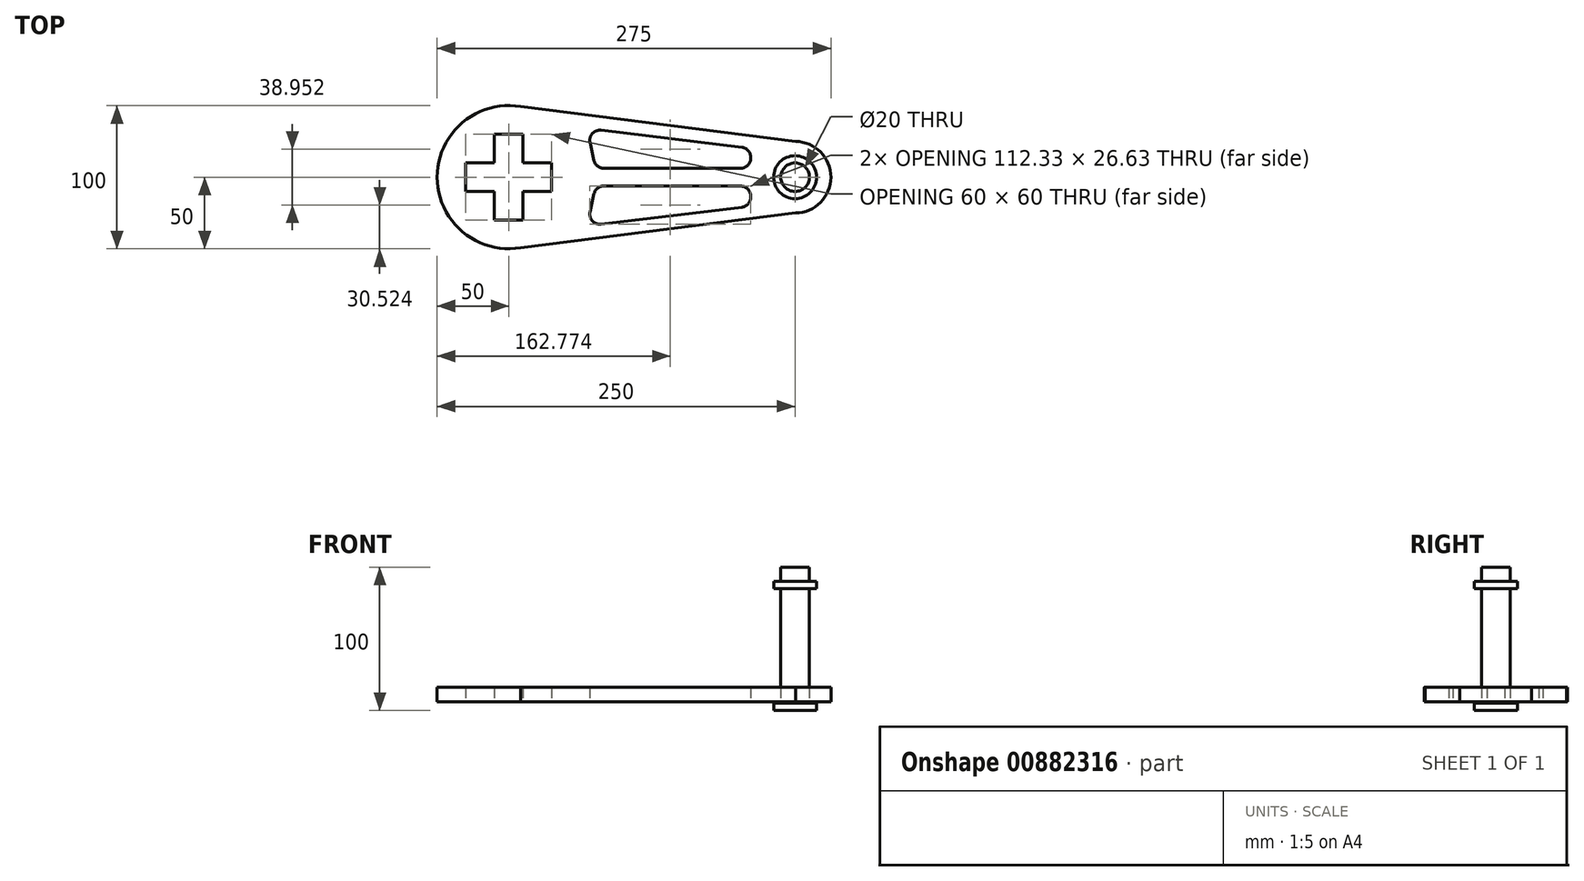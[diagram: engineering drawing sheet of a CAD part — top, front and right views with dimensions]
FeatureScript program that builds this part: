
annotation { "Feature Type Name" : "Feature", "Feature Type Description" : "" }
export const myFeature = defineFeature(function(context is Context, id is Id, definition is map)
    precondition{}
    {
        {
            var Q0;
            Q0=qCreatedBy(makeId("Top.planeOp"),FACE);
            var sketch = newSketch(context, id + "F0", { "sketchPlane" : qUnion([Q0])});
            skCircle(sketch, "E0", {"center": v(0, 0) * mm, "radius": 50 * mm});
            skLineSegment(sketch, "E1", {"start": v(0, 0) * mm, "end": v(0, 30) * mm, "construction": true});
            skLineSegment(sketch, "E2", {"start": v(0, 0) * mm, "end": v(-33.4, 0) * mm, "construction": true});
            skLineSegment(sketch, "E3", {"start": v(0, 30) * mm, "end": v(-10, 30) * mm});
            skLineSegment(sketch, "E4", {"start": v(-10, 30) * mm, "end": v(-10, 10) * mm});
            skLineSegment(sketch, "E5", {"start": v(-10, 10) * mm, "end": v(-30, 10) * mm});
            skLineSegment(sketch, "E6", {"start": v(-30, 10) * mm, "end": v(-30, 0) * mm});
            skLineSegment(sketch, "E7.MirrorCS", {"start": v(0, 30) * mm, "end": v(10, 30) * mm});
            skLineSegment(sketch, "E8.MirrorCS", {"start": v(10, 30) * mm, "end": v(10, 10) * mm});
            skLineSegment(sketch, "E9.MirrorCS", {"start": v(10, 10) * mm, "end": v(30, 10) * mm});
            skLineSegment(sketch, "E10.MirrorCS", {"start": v(30, 10) * mm, "end": v(30, 0) * mm});
            skLineSegment(sketch, "E11.MirrorCS", {"start": v(-30, -10) * mm, "end": v(-30, 0) * mm});
            skLineSegment(sketch, "E12.MirrorCS", {"start": v(-10, -10) * mm, "end": v(-30, -10) * mm});
            skLineSegment(sketch, "E13.MirrorCS", {"start": v(-10, -30) * mm, "end": v(-10, -10) * mm});
            skLineSegment(sketch, "E14.MirrorCS", {"start": v(0, -30) * mm, "end": v(-10, -30) * mm});
            skLineSegment(sketch, "E15.MirrorCS", {"start": v(0, -30) * mm, "end": v(10, -30) * mm});
            skLineSegment(sketch, "E16.MirrorCS", {"start": v(10, -30) * mm, "end": v(10, -10) * mm});
            skLineSegment(sketch, "E17.MirrorCS", {"start": v(10, -10) * mm, "end": v(30, -10) * mm});
            skLineSegment(sketch, "E18.MirrorCS", {"start": v(30, -10) * mm, "end": v(30, 0) * mm});
            skCircle(sketch, "E19", {"center": v(200, 0) * mm, "radius": 25 * mm});
            skLineSegment(sketch, "E20", {"start": v(8.22, 49.32) * mm, "end": v(200.26, 25) * mm});
            skLineSegment(sketch, "E21.MirrorCS", {"start": v(8.22, -49.32) * mm, "end": v(200.26, -25) * mm});
            skCircle(sketch, "E22", {"center": v(200, 0) * mm, "radius": 10 * mm});
            skLineSegment(sketch, "E23", {"start": v(56.77, 24.35) * mm, "end": v(59.53, 11.67) * mm});
            skLineSegment(sketch, "E24", {"start": v(66.37, 6.16) * mm, "end": v(161.94, 6.16) * mm});
            skLineSegment(sketch, "E25", {"start": v(168.94, 13.16) * mm, "end": v(168.94, 13.98) * mm});
            skLineSegment(sketch, "E26", {"start": v(162.78, 20.93) * mm, "end": v(64.44, 32.8) * mm});
            skPoint(sketch, "E27.visualSharp", {"position": v(54.67, 33.97) * mm});
            skArc(sketch, "E27.filletArc", {"start": v(64.44, 32.8) * mm, "mid": v(58.43, 30.55) * mm, "end": v(56.77, 24.35) * mm});
            skPoint(sketch, "E28.visualSharp", {"position": v(168.94, 20.2) * mm});
            skArc(sketch, "E28.filletArc", {"start": v(168.94, 13.98) * mm, "mid": v(167.18, 18.63) * mm, "end": v(162.78, 20.93) * mm});
            skPoint(sketch, "E29.visualSharp", {"position": v(168.94, 6.16) * mm});
            skArc(sketch, "E29.filletArc", {"start": v(161.94, 6.16) * mm, "mid": v(166.9, 8.21) * mm, "end": v(168.94, 13.16) * mm});
            skPoint(sketch, "E30.visualSharp", {"position": v(60.72, 6.16) * mm});
            skArc(sketch, "E30.filletArc", {"start": v(59.53, 11.67) * mm, "mid": v(61.97, 7.7) * mm, "end": v(66.37, 6.16) * mm});
            skLineSegment(sketch, "E31.MirrorCS", {"start": v(66.37, -6.16) * mm, "end": v(161.94, -6.16) * mm});
            skArc(sketch, "E32.MirrorCS", {"start": v(59.53, -11.67) * mm, "mid": v(61.97, -7.7) * mm, "end": v(66.37, -6.16) * mm});
            skLineSegment(sketch, "E33.MirrorCS", {"start": v(56.77, -24.35) * mm, "end": v(59.53, -11.67) * mm});
            skArc(sketch, "E34.MirrorCS", {"start": v(64.44, -32.8) * mm, "mid": v(58.43, -30.55) * mm, "end": v(56.77, -24.35) * mm});
            skLineSegment(sketch, "E35.MirrorCS", {"start": v(162.78, -20.93) * mm, "end": v(64.44, -32.8) * mm});
            skArc(sketch, "E36.MirrorCS", {"start": v(168.94, -13.98) * mm, "mid": v(167.18, -18.63) * mm, "end": v(162.78, -20.93) * mm});
            skLineSegment(sketch, "E37.MirrorCS", {"start": v(168.94, -13.16) * mm, "end": v(168.94, -13.98) * mm});
            skArc(sketch, "E38.MirrorCS", {"start": v(161.94, -6.16) * mm, "mid": v(166.9, -8.21) * mm, "end": v(168.94, -13.16) * mm});
            skSolve(sketch);
        }
        {
            var Q0;
            Q0=qSketchRegion(id+"F0",true);
            extrude(context, id + "F1", {"entities" : qUnion([Q0]), "depth" : 10 * mm, "offsetDistance" : 25 * mm});
        }
        {
            var Q0;
            Q0=makeQuery(id+"F1.opExtrude","CAP_FACE",FACE,{"disambiguationData":[OSD([sQuery(id+"F0.wireOp",EDGE,"E0"),sQuery(id+"F0.wireOp",EDGE,"E3"),sQuery(id+"F0.wireOp",EDGE,"E4"),sQuery(id+"F0.wireOp",EDGE,"E5"),sQuery(id+"F0.wireOp",EDGE,"E6"),sQuery(id+"F0.wireOp",EDGE,"E7.MirrorCS"),sQuery(id+"F0.wireOp",EDGE,"E8.MirrorCS"),sQuery(id+"F0.wireOp",EDGE,"E9.MirrorCS"),sQuery(id+"F0.wireOp",EDGE,"E10.MirrorCS"),sQuery(id+"F0.wireOp",EDGE,"E11.MirrorCS"),sQuery(id+"F0.wireOp",EDGE,"E12.MirrorCS"),sQuery(id+"F0.wireOp",EDGE,"E13.MirrorCS"),sQuery(id+"F0.wireOp",EDGE,"E14.MirrorCS"),sQuery(id+"F0.wireOp",EDGE,"E15.MirrorCS"),sQuery(id+"F0.wireOp",EDGE,"E16.MirrorCS"),sQuery(id+"F0.wireOp",EDGE,"E17.MirrorCS"),sQuery(id+"F0.wireOp",EDGE,"E18.MirrorCS"),sQuery(id+"F0.wireOp",EDGE,"E19"),sQuery(id+"F0.wireOp",EDGE,"E20"),sQuery(id+"F0.wireOp",EDGE,"E21.MirrorCS"),sQuery(id+"F0.wireOp",EDGE,"E22"),sQuery(id+"F0.wireOp",EDGE,"E23"),sQuery(id+"F0.wireOp",EDGE,"E24"),sQuery(id+"F0.wireOp",EDGE,"E25"),sQuery(id+"F0.wireOp",EDGE,"E26"),sQuery(id+"F0.wireOp",EDGE,"E27.filletArc"),sQuery(id+"F0.wireOp",EDGE,"E28.filletArc"),sQuery(id+"F0.wireOp",EDGE,"E29.filletArc"),sQuery(id+"F0.wireOp",EDGE,"E30.filletArc"),sQuery(id+"F0.wireOp",EDGE,"E31.MirrorCS"),sQuery(id+"F0.wireOp",EDGE,"E32.MirrorCS"),sQuery(id+"F0.wireOp",EDGE,"E33.MirrorCS"),sQuery(id+"F0.wireOp",EDGE,"E34.MirrorCS"),sQuery(id+"F0.wireOp",EDGE,"E35.MirrorCS"),sQuery(id+"F0.wireOp",EDGE,"E36.MirrorCS"),sQuery(id+"F0.wireOp",EDGE,"E37.MirrorCS"),sQuery(id+"F0.wireOp",EDGE,"E38.MirrorCS")])],"isStart":false});
            var sketch = newSketch(context, id + "F2", { "sketchPlane" : qUnion([Q0])});
            skCircle(sketch, "E39", {"center": v(200, 0) * mm, "radius": 10 * mm});
            skSolve(sketch);
        }
        {
            var Q0;
            Q0=qSketchRegion(id+"F2",true);
            extrude(context, id + "F3", {"entities" : qUnion([Q0]), "depth" : 100 * mm, "offsetDistance" : 25 * mm});
        }
        {
            var Q0;
            Q0=makeQuery(id+"F3.opExtrude","SWEPT_BODY",BODY,{"disambiguationData":[OSD([sQuery(id+"F2.wireOp",EDGE,"E39")])]});
            transform(context, id + "F4", {"entities" : qUnion([Q0]), "transformType" : TransformType.TRANSLATION_3D, "dx" : 0 * mm, "dy" : 0 * mm, "dz" : -16 * mm, "makeCopy" : false});
        }
        {
            var Q0;
            Q0=makeQuery(id+"F3.opExtrude","CAP_FACE",FACE,{"disambiguationData":[OSD([sQuery(id+"F2.wireOp",EDGE,"E39")])],"isStart":true});
            var sketch = newSketch(context, id + "F5", { "sketchPlane" : qUnion([Q0])});
            skCircle(sketch, "E40", {"center": v(200, 0) * mm, "radius": 10 * mm});
            skCircle(sketch, "E41", {"center": v(200, 0) * mm, "radius": 15 * mm});
            skSolve(sketch);
        }
        {
            var Q0;
            Q0 = qSketchRegion(id + "F5", true);
            extrude(context, id + "F6", {"entities" : qUnion([Q0]), "operationType" : NewBodyOperationType.ADD, "oppositeDirection" : true, "depth" : 5 * mm, "offsetDistance" : 25 * mm});
        }
        {
            var Q0;
            Q0=makeQuery(id+"F3.opExtrude","CAP_FACE",FACE,{"disambiguationData":[OSD([sQuery(id+"F2.wireOp",EDGE,"E39")])],"isStart":false});
            cPlane(context, id + "F7", {"entities" : qUnion([Q0]), "cplaneType" : CPlaneType.OFFSET, "offset" : 10 * mm, "oppositeDirection" : true, "width" : 150 * mm, "height" : 150 * mm});
        }
        {
            var Q0;
            Q0=qCreatedBy(id+"F7.planeOp",FACE);
            var sketch = newSketch(context, id + "F8", { "sketchPlane" : qUnion([Q0])});
            skCircle(sketch, "E42", {"center": v(200, 0) * mm, "radius": 10 * mm});
            skCircle(sketch, "E43", {"center": v(200, 0) * mm, "radius": 15 * mm});
            skSolve(sketch);
        }
        {
            var Q0;
            Q0 = qSketchRegion(id + "F8", true);
            extrude(context, id + "F9", {"entities" : qUnion([Q0]), "operationType" : NewBodyOperationType.ADD, "oppositeDirection" : true, "depth" : 5 * mm, "offsetDistance" : 25 * mm});
        }
    });
